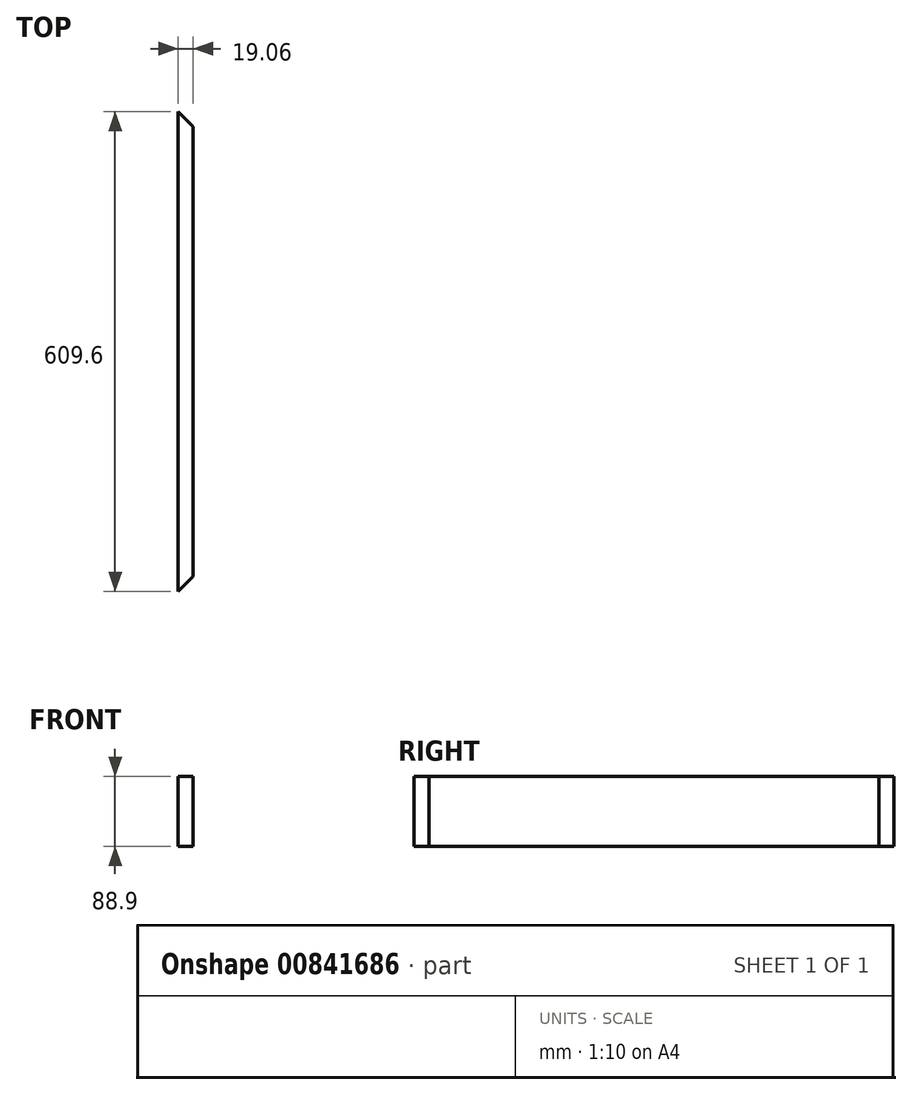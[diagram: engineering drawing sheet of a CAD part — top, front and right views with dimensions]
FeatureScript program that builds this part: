
annotation { "Feature Type Name" : "Feature", "Feature Type Description" : "" }
export const myFeature = defineFeature(function(context is Context, id is Id, definition is map)
    precondition{}
    {
        {
            var Q0;
            Q0=qCreatedBy(makeId("Front.planeOp"),FACE);
            var sketch = newSketch(context, id + "F0", { "sketchPlane" : qUnion([Q0])});
            skLineSegment(sketch, "E0.bottom", {"start": v(9.53, -44.45) * mm, "end": v(-9.52, -44.45) * mm});
            skLineSegment(sketch, "E0.top", {"start": v(9.53, 44.45) * mm, "end": v(-9.52, 44.45) * mm});
            skLineSegment(sketch, "E0.left", {"start": v(9.53, -44.45) * mm, "end": v(9.53, 44.45) * mm});
            skLineSegment(sketch, "E0.right", {"start": v(-9.52, -44.45) * mm, "end": v(-9.52, 44.45) * mm});
            skPoint(sketch, "E0.middle", {"position": v(0, 0) * mm});
            skSolve(sketch);
        }
        {
            var Q0;
            Q0=makeQuery(id+"F0.imprint","IMPRINT",FACE,{"disambiguationData":[TD([[makeQuery(id+"F0.imprint","IMPRINT",EDGE,{"derivedFrom":sQuery(id+"F0.wireOp",EDGE,"E0.bottom")}),-1.0]])]});
            extrude(context, id + "F1", {"entities" : qUnion([Q0]), "depth" : 609.6 * mm, "offsetDistance" : 25.4 * mm});
        }
        {
            var Q0;
            Q0=makeQuery(id+"F1.opExtrude","SWEPT_FACE",FACE,{"disambiguationData":[OSD([sQuery(id+"F0.wireOp",EDGE,"E0.top")])]});
            var sketch = newSketch(context, id + "F2", { "sketchPlane" : qUnion([Q0])});
            skLineSegment(sketch, "E1", {"start": v(-9.52, 0) * mm, "end": v(9.53, -19.05) * mm});
            skLineSegment(sketch, "E2", {"start": v(9.53, -19.05) * mm, "end": v(9.53, 0) * mm});
            skLineSegment(sketch, "E3", {"start": v(9.53, 0) * mm, "end": v(-9.52, 0) * mm});
            skLineSegment(sketch, "E4", {"start": v(-9.53, -609.6) * mm, "end": v(9.52, -590.55) * mm});
            skLineSegment(sketch, "E5", {"start": v(9.52, -590.55) * mm, "end": v(9.53, -609.6) * mm});
            skSolve(sketch);
        }
        {
            var Q0;
            Q0=makeQuery(id+"F2.imprint","IMPRINT",FACE,{"disambiguationData":[TD([[makeQuery(id+"F2.imprint","IMPRINT",EDGE,{"derivedFrom":sQuery(id+"F2.wireOp",EDGE,"E4")}),-1.0]])]});
            var Q1;
            Q1=makeQuery(id+"F2.imprint","IMPRINT",FACE,{"disambiguationData":[TD([[makeQuery(id+"F2.imprint","IMPRINT",EDGE,{"derivedFrom":sQuery(id+"F2.wireOp",EDGE,"E1")}),1.0]])]});
            extrude(context, id + "F3", {"entities" : qUnion([Q0, Q1]), "operationType" : NewBodyOperationType.REMOVE, "endBound" : BoundingType.THROUGH_ALL, "oppositeDirection" : true, "depth" : 25.4 * mm, "offsetDistance" : 25.4 * mm});
        }
    });
